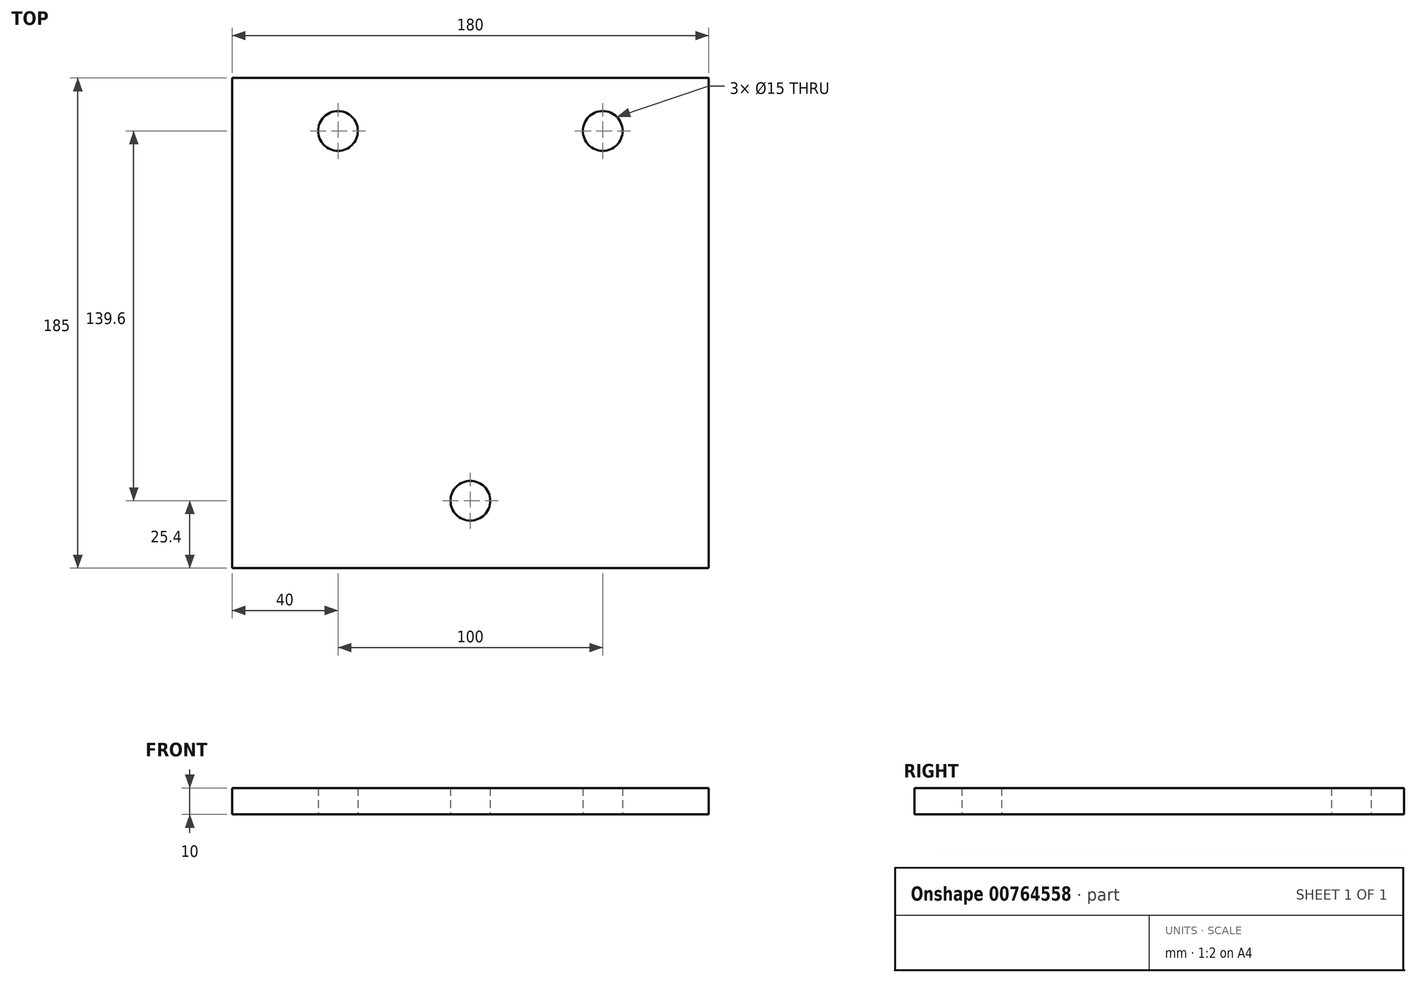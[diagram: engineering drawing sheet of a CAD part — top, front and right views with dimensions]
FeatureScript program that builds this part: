
annotation { "Feature Type Name" : "Feature", "Feature Type Description" : "" }
export const myFeature = defineFeature(function(context is Context, id is Id, definition is map)
    precondition{}
    {
        {
            var Q0;
            Q0=qCreatedBy(makeId("Top.planeOp"),FACE);
            var sketch = newSketch(context, id + "F0", { "sketchPlane" : qUnion([Q0])});
            skLineSegment(sketch, "E0.bottom", {"start": v(90, 92.5) * mm, "end": v(-90, 92.5) * mm});
            skLineSegment(sketch, "E0.top", {"start": v(90, -92.5) * mm, "end": v(-90, -92.5) * mm});
            skLineSegment(sketch, "E0.left", {"start": v(90, 92.5) * mm, "end": v(90, -92.5) * mm});
            skLineSegment(sketch, "E0.right", {"start": v(-90, 92.5) * mm, "end": v(-90, -92.5) * mm});
            skPoint(sketch, "E0.middle", {"position": v(0, 0) * mm});
            skCircle(sketch, "E1", {"center": v(0, -67.1) * mm, "radius": 7.5 * mm});
            skCircle(sketch, "E2", {"center": v(-50, 72.5) * mm, "radius": 7.5 * mm});
            skCircle(sketch, "E3", {"center": v(50, 72.5) * mm, "radius": 7.5 * mm});
            skSolve(sketch);
        }
        {
            var Q0;
            Q0=makeQuery(id+"F0.imprint","IMPRINT",FACE,{"disambiguationData":[TD([[makeQuery(id+"F0.imprint","IMPRINT",EDGE,{"derivedFrom":sQuery(id+"F0.wireOp",EDGE,"E0.bottom")}),1.0]])]});
            extrude(context, id + "F1", {"entities" : qUnion([Q0]), "depth" : 10 * mm, "offsetDistance" : 25 * mm});
        }
    });
